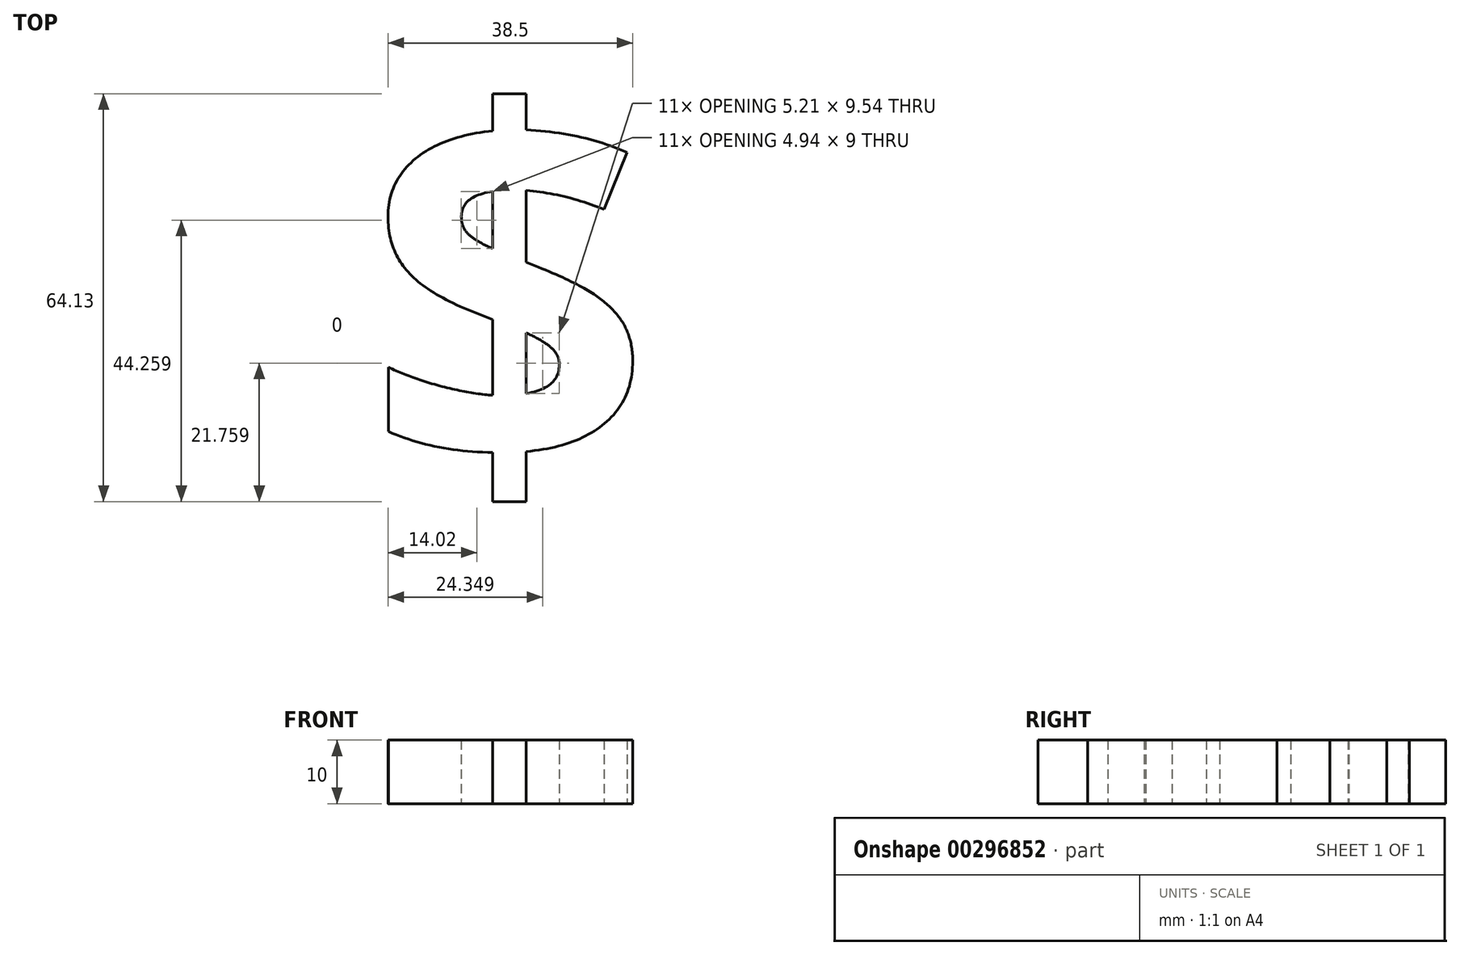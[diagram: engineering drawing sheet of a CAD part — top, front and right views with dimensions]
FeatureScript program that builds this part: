
annotation { "Feature Type Name" : "Feature", "Feature Type Description" : "" }
export const myFeature = defineFeature(function(context is Context, id is Id, definition is map)
    precondition{}
    {
        {
            var Q0;
            Q0=qCreatedBy(makeId("Top.planeOp"),FACE);
            var sketch = newSketch(context, id + "F0", { "sketchPlane" : qUnion([Q0])});
            skText(sketch, "E0", { "text": "$", "fontName": "OpenSans-Bold.ttf"});
            const initialGuessF0  = {"E0": [0, 0, 1, 0, 0.05653]};
            skSetInitialGuess(sketch, initialGuessF0);
            skSolve(sketch);
        }
        {
            var Q0;
            Q0=makeQuery(id+"F0.imprint","IMPRINT",FACE,{"disambiguationData":[TD([[makeQuery(id+"F0.imprint","IMPRINT",EDGE,{"derivedFrom":sQuery(id+"F0.wireOp",EDGE,"E0.sketch_text.stroke-0")}),-1.0]])]});
            extrude(context, id + "F1", {"entities" : qUnion([Q0]), "depth" : 10 * mm});
        }
    });
